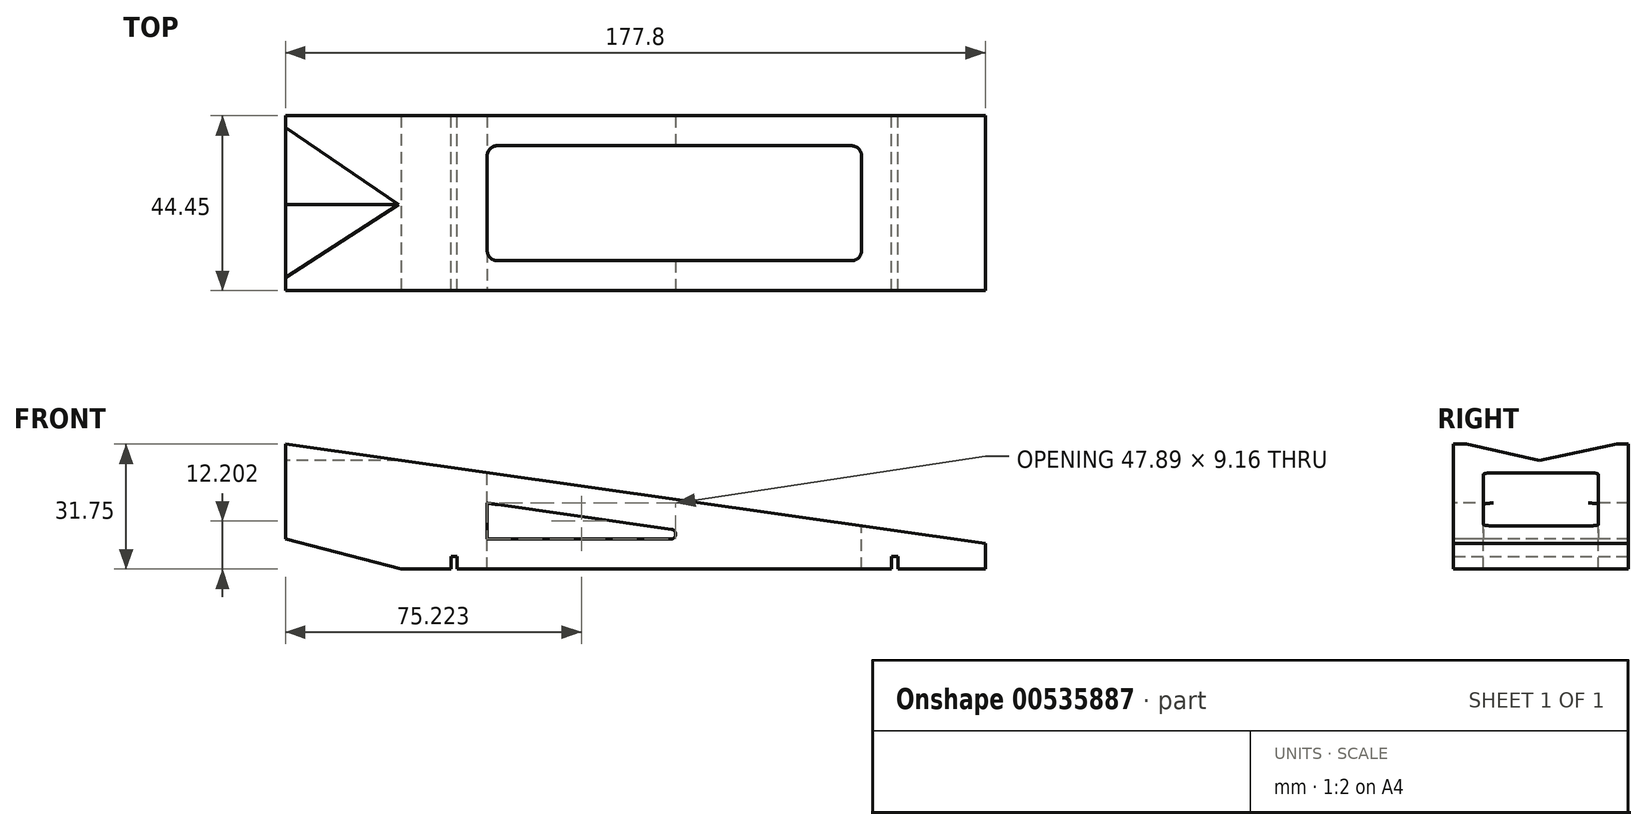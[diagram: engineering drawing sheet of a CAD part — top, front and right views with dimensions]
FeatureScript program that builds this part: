
annotation { "Feature Type Name" : "Feature", "Feature Type Description" : "" }
export const myFeature = defineFeature(function(context is Context, id is Id, definition is map)
    precondition{}
    {
        {
            var Q0;
            Q0=qCreatedBy(makeId("Top.planeOp"),FACE);
            var sketch = newSketch(context, id + "F0", { "sketchPlane" : qUnion([Q0])});
            skLineSegment(sketch, "E0.bottom", {"start": v(0, 0) * mm, "end": v(-177.8, 0) * mm});
            skLineSegment(sketch, "E0.top", {"start": v(0, -44.45) * mm, "end": v(-177.8, -44.45) * mm});
            skLineSegment(sketch, "E0.left", {"start": v(0, 0) * mm, "end": v(0, -44.45) * mm});
            skLineSegment(sketch, "E0.right", {"start": v(-177.8, 0) * mm, "end": v(-177.8, -44.45) * mm});
            skSolve(sketch);
        }
        {
            var Q0;
            Q0=makeQuery(id+"F0.imprint","IMPRINT",FACE,{"disambiguationData":[TD([[makeQuery(id+"F0.imprint","IMPRINT",EDGE,{"derivedFrom":sQuery(id+"F0.wireOp",EDGE,"E0.bottom")}),1.0]])]});
            extrude(context, id + "F1", {"entities" : qUnion([Q0]), "depth" : 31.75 * mm});
        }
        {
            var Q0;
            Q0=makeQuery(id+"F1.opExtrude","CAP_FACE",FACE,{"disambiguationData":[OSD([sQuery(id+"F0.wireOp",EDGE,"E0.bottom"),sQuery(id+"F0.wireOp",EDGE,"E0.top"),sQuery(id+"F0.wireOp",EDGE,"E0.left"),sQuery(id+"F0.wireOp",EDGE,"E0.right")])],"isStart":true});
            var sketch = newSketch(context, id + "F2", { "sketchPlane" : qUnion([Q0])});
            skLineSegment(sketch, "E1.bottom", {"start": v(-135.73, 44.45) * mm, "end": v(-134.14, 44.45) * mm});
            skLineSegment(sketch, "E1.top", {"start": v(-135.73, 0) * mm, "end": v(-134.14, 0) * mm});
            skLineSegment(sketch, "E1.left", {"start": v(-135.73, 44.45) * mm, "end": v(-135.73, 0) * mm});
            skLineSegment(sketch, "E1.right", {"start": v(-134.14, 44.45) * mm, "end": v(-134.14, 0) * mm});
            skLineSegment(sketch, "E2.bottom", {"start": v(-23.81, 44.45) * mm, "end": v(-22.23, 44.45) * mm});
            skLineSegment(sketch, "E2.top", {"start": v(-23.81, 0) * mm, "end": v(-22.23, 0) * mm});
            skLineSegment(sketch, "E2.left", {"start": v(-23.81, 44.45) * mm, "end": v(-23.81, 0) * mm});
            skLineSegment(sketch, "E2.right", {"start": v(-22.23, 44.45) * mm, "end": v(-22.23, 0) * mm});
            skSolve(sketch);
        }
        {
            var Q0;
            Q0=makeQuery(id+"F2.imprint","IMPRINT",FACE,{"disambiguationData":[TD([[makeQuery(id+"F2.imprint","IMPRINT",EDGE,{"derivedFrom":sQuery(id+"F2.wireOp",EDGE,"E2.bottom")}),1.0]])]});
            var Q1;
            Q1=makeQuery(id+"F2.imprint","IMPRINT",FACE,{"disambiguationData":[TD([[makeQuery(id+"F2.imprint","IMPRINT",EDGE,{"derivedFrom":sQuery(id+"F2.wireOp",EDGE,"E1.bottom")}),1.0]])]});
            extrude(context, id + "F3", {"entities" : qUnion([Q0, Q1]), "operationType" : NewBodyOperationType.REMOVE, "oppositeDirection" : true, "depth" : 3.17 * mm});
        }
        {
            var Q0;
            Q0=makeQuery(id+"F1.opExtrude","CAP_FACE",FACE,{"disambiguationData":[OSD([sQuery(id+"F0.wireOp",EDGE,"E0.bottom"),sQuery(id+"F0.wireOp",EDGE,"E0.top"),sQuery(id+"F0.wireOp",EDGE,"E0.left"),sQuery(id+"F0.wireOp",EDGE,"E0.right")])],"isStart":false});
            var sketch = newSketch(context, id + "F4", { "sketchPlane" : qUnion([Q0])});
            skLineSegment(sketch, "E3.bottom", {"start": v(-31.43, -7.62) * mm, "end": v(-126.52, -7.62) * mm});
            skLineSegment(sketch, "E3.top", {"start": v(-31.43, -36.83) * mm, "end": v(-126.52, -36.83) * mm});
            skLineSegment(sketch, "E3.left", {"start": v(-31.43, -7.62) * mm, "end": v(-31.43, -36.83) * mm});
            skLineSegment(sketch, "E3.right", {"start": v(-126.52, -7.62) * mm, "end": v(-126.52, -36.83) * mm});
            skSolve(sketch);
        }
        {
            var Q0;
            Q0=makeQuery(id+"F4.imprint","IMPRINT",FACE,{"disambiguationData":[TD([[makeQuery(id+"F4.imprint","IMPRINT",EDGE,{"derivedFrom":sQuery(id+"F4.wireOp",EDGE,"E3.bottom")}),1.0]])]});
            extrude(context, id + "F5", {"entities" : qUnion([Q0]), "operationType" : NewBodyOperationType.REMOVE, "endBound" : BoundingType.THROUGH_ALL, "oppositeDirection" : true, "depth" : 25.4 * mm, "offsetDistance" : 25.4 * mm});
        }
        {
            var Q0;
            Q0=makeQuery(id+"F1.opExtrude","SWEPT_FACE",FACE,{"disambiguationData":[OSD([sQuery(id+"F0.wireOp",EDGE,"E0.top")])]});
            var sketch = newSketch(context, id + "F6", { "sketchPlane" : qUnion([Q0])});
            skLineSegment(sketch, "E4", {"start": v(0, 6.54) * mm, "end": v(-177.8, 31.75) * mm});
            skLineSegment(sketch, "E5", {"start": v(-177.8, 31.75) * mm, "end": v(0, 31.75) * mm});
            skLineSegment(sketch, "E6", {"start": v(0, 31.75) * mm, "end": v(0, 6.54) * mm});
            skSolve(sketch);
        }
        {
            var Q0;
            Q0 = qSketchRegion(id + "F6", true);
            extrude(context, id + "F7", {"entities" : qUnion([Q0]), "operationType" : NewBodyOperationType.REMOVE, "endBound" : BoundingType.THROUGH_ALL, "oppositeDirection" : true, "depth" : 25.4 * mm, "offsetDistance" : 25.4 * mm});
        }
        {
            var Q0;
            Q0=makeQuery(id+"F1.opExtrude","SWEPT_FACE",FACE,{"disambiguationData":[OSD([sQuery(id+"F0.wireOp",EDGE,"E0.top")])]});
            var sketch = newSketch(context, id + "F8", { "sketchPlane" : qUnion([Q0])});
            skLineSegment(sketch, "E7", {"start": v(-126.52, 7.62) * mm, "end": v(-126.52, 16.78) * mm});
            skLineSegment(sketch, "E8", {"start": v(-126.52, 16.78) * mm, "end": v(-79.72, 10.15) * mm});
            skLineSegment(sketch, "E9", {"start": v(-79.9, 7.62) * mm, "end": v(-126.52, 7.62) * mm});
            skPoint(sketch, "E10.visualSharp", {"position": v(-61.9, 7.62) * mm});
            skArc(sketch, "E10.filletArc", {"start": v(-79.9, 7.62) * mm, "mid": v(-78.63, 8.8) * mm, "end": v(-79.72, 10.15) * mm});
            skSolve(sketch);
        }
        {
            var Q0;
            Q0 = qSketchRegion(id + "F8", true);
            extrude(context, id + "F9", {"entities" : qUnion([Q0]), "operationType" : NewBodyOperationType.REMOVE, "endBound" : BoundingType.THROUGH_ALL, "oppositeDirection" : true, "depth" : 25.4 * mm, "offsetDistance" : 25.4 * mm});
        }
        {
            var Q0;
            Q0=makeQuery(id+"F1.opExtrude","SWEPT_FACE",FACE,{"disambiguationData":[OSD([sQuery(id+"F0.wireOp",EDGE,"E0.top")])]});
            var sketch = newSketch(context, id + "F10", { "sketchPlane" : qUnion([Q0])});
            skLineSegment(sketch, "E11", {"start": v(-148.43, 0) * mm, "end": v(-177.8, 7.62) * mm});
            skLineSegment(sketch, "E12", {"start": v(-177.8, 7.62) * mm, "end": v(-177.8, 0) * mm});
            skLineSegment(sketch, "E13", {"start": v(-177.8, 0) * mm, "end": v(-148.43, 0) * mm});
            skSolve(sketch);
        }
        {
            var Q0;
            Q0 = qSketchRegion(id + "F10", true);
            extrude(context, id + "F11", {"entities" : qUnion([Q0]), "operationType" : NewBodyOperationType.REMOVE, "endBound" : BoundingType.THROUGH_ALL, "oppositeDirection" : true, "depth" : 25.4 * mm, "offsetDistance" : 25.4 * mm});
        }
        {
            var Q0;
            Q0=makeQuery(id+"F1.opExtrude","SWEPT_FACE",FACE,{"disambiguationData":[OSD([sQuery(id+"F0.wireOp",EDGE,"E0.right")])]});
            var sketch = newSketch(context, id + "F12", { "sketchPlane" : qUnion([Q0])});
            skLineSegment(sketch, "E14", {"start": v(2.96, 31.75) * mm, "end": v(22.57, 27.67) * mm});
            skLineSegment(sketch, "E15", {"start": v(22.57, 27.67) * mm, "end": v(41.12, 31.75) * mm});
            skLineSegment(sketch, "E16", {"start": v(41.12, 31.75) * mm, "end": v(2.96, 31.75) * mm});
            skSolve(sketch);
        }
        {
            var Q0;
            Q0 = qSketchRegion(id + "F12", true);
            extrude(context, id + "F13", {"entities" : qUnion([Q0]), "operationType" : NewBodyOperationType.REMOVE, "endBound" : BoundingType.THROUGH_ALL, "oppositeDirection" : true, "depth" : 25.4 * mm, "offsetDistance" : 25.4 * mm});
        }
        {
            var Q0;
            Q0=makeQuery(id+"F5.boolean.opBoolean","COPY",EDGE,{"derivedFrom":makeQuery(id+"F5.opExtrude","SWEPT_EDGE",EDGE,{"disambiguationData":[OSD([sQuery(id+"F4.wireOp",EDGE,"E3.top"),sQuery(id+"F4.wireOp",EDGE,"E3.left")])]})});
            var Q1;
            {var subQ0=sQuery(id+"F4.wireOp",EDGE,"E3.right");var subQ1=sQuery(id+"F4.wireOp",EDGE,"E3.top");Q1=makeQuery(id+"F9.boolean.opBoolean","SPLIT",EDGE,{"disambiguationData":[TD([makeQuery(id+"F7.boolean.opBoolean","COPY",FACE,{"derivedFrom":makeQuery(id+"F7.opExtrude","SWEPT_FACE",FACE,{"disambiguationData":[OSD([sQuery(id+"F6.wireOp",EDGE,"E4")])]})})])],"derivedFrom":makeQuery(id+"F5.boolean.opBoolean","COPY",EDGE,{"derivedFrom":makeQuery(id+"F5.opExtrude","SWEPT_EDGE",EDGE,{"disambiguationData":[OSD([subQ1,subQ0])]})})});}
            var Q2;
            {var subQ0=sQuery(id+"F4.wireOp",EDGE,"E3.top");var subQ1=sQuery(id+"F4.wireOp",EDGE,"E3.right");Q2=makeQuery(id+"F9.boolean.opBoolean","SPLIT",EDGE,{"disambiguationData":[TD([makeQuery(id+"F9.opExtrude","SWEPT_FACE",FACE,{"disambiguationData":[OSD([sQuery(id+"F8.wireOp",EDGE,"E9")])]})])],"derivedFrom":makeQuery(id+"F5.boolean.opBoolean","COPY",EDGE,{"derivedFrom":makeQuery(id+"F5.opExtrude","SWEPT_EDGE",EDGE,{"disambiguationData":[OSD([subQ0,subQ1])]})})});}
            var Q3;
            {var subQ0=sQuery(id+"F4.wireOp",EDGE,"E3.right");var subQ1=sQuery(id+"F4.wireOp",EDGE,"E3.bottom");Q3=makeQuery(id+"F9.boolean.opBoolean","SPLIT",EDGE,{"disambiguationData":[TD([makeQuery(id+"F7.boolean.opBoolean","COPY",FACE,{"derivedFrom":makeQuery(id+"F7.opExtrude","SWEPT_FACE",FACE,{"disambiguationData":[OSD([sQuery(id+"F6.wireOp",EDGE,"E4")])]})})])],"derivedFrom":makeQuery(id+"F5.boolean.opBoolean","COPY",EDGE,{"derivedFrom":makeQuery(id+"F5.opExtrude","SWEPT_EDGE",EDGE,{"disambiguationData":[OSD([subQ1,subQ0])]})})});}
            var Q4;
            {var subQ0=sQuery(id+"F4.wireOp",EDGE,"E3.bottom");var subQ1=sQuery(id+"F4.wireOp",EDGE,"E3.right");Q4=makeQuery(id+"F9.boolean.opBoolean","SPLIT",EDGE,{"disambiguationData":[TD([makeQuery(id+"F9.opExtrude","SWEPT_FACE",FACE,{"disambiguationData":[OSD([sQuery(id+"F8.wireOp",EDGE,"E9")])]})])],"derivedFrom":makeQuery(id+"F5.boolean.opBoolean","COPY",EDGE,{"derivedFrom":makeQuery(id+"F5.opExtrude","SWEPT_EDGE",EDGE,{"disambiguationData":[OSD([subQ0,subQ1])]})})});}
            var Q5;
            Q5=makeQuery(id+"F5.boolean.opBoolean","COPY",EDGE,{"derivedFrom":makeQuery(id+"F5.opExtrude","SWEPT_EDGE",EDGE,{"disambiguationData":[OSD([sQuery(id+"F4.wireOp",EDGE,"E3.bottom"),sQuery(id+"F4.wireOp",EDGE,"E3.left")])]})});
            fillet(context, id + "F14", {"entities" : qUnion([Q0, Q1, Q2, Q3, Q4, Q5]), "radius" : 2.54 * mm, "tangentPropagation" : true, "allowEdgeOverflow" : false});
        }
    });
